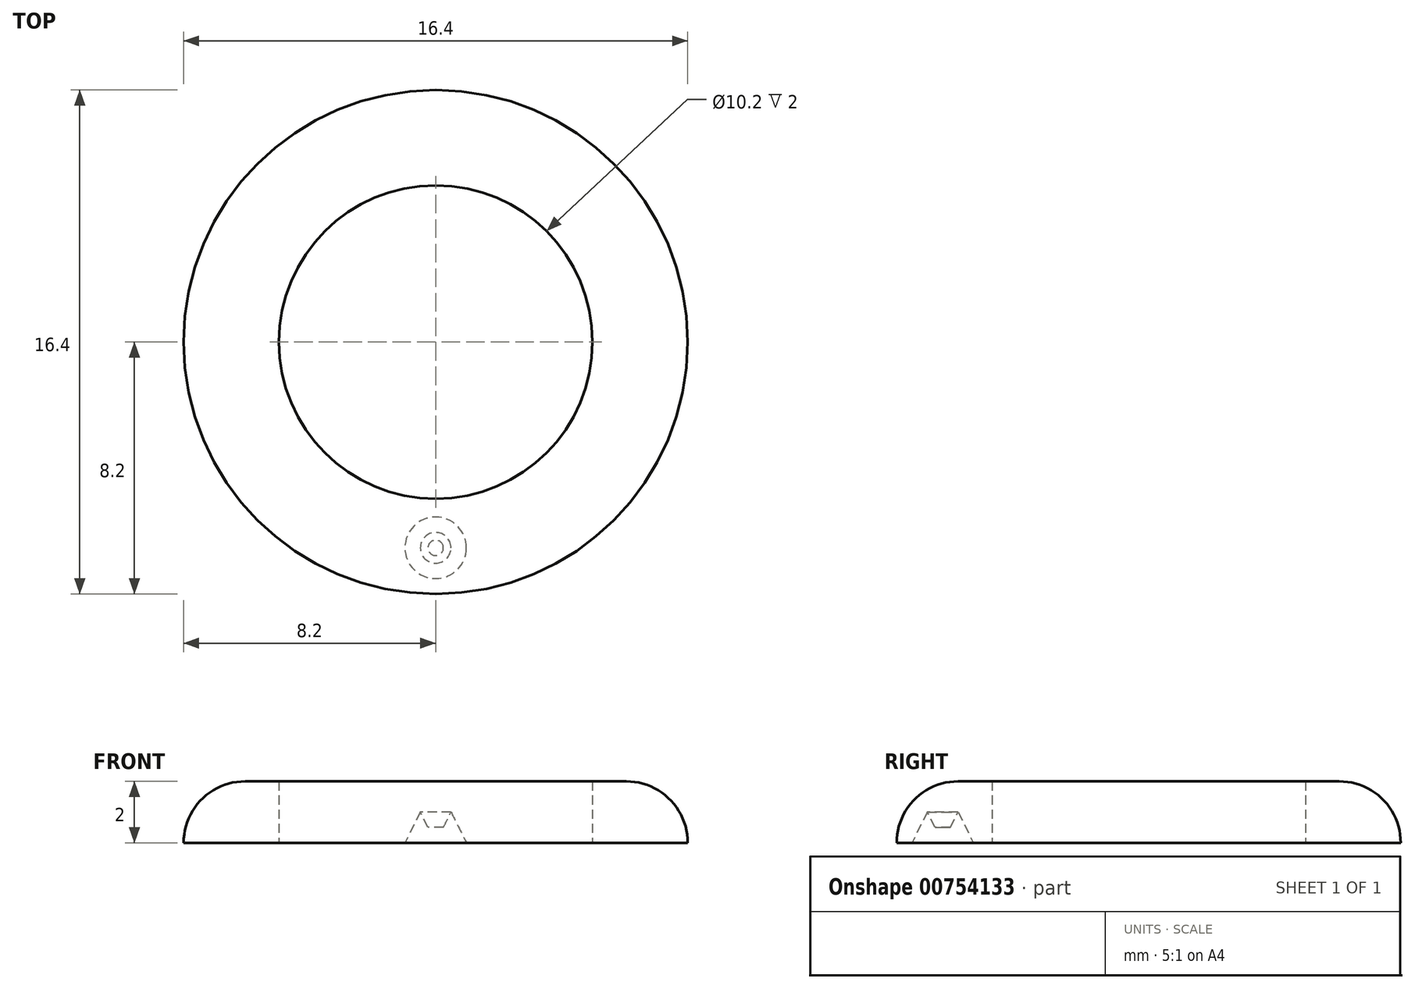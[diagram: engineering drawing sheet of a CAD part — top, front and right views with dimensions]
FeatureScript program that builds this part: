
annotation { "Feature Type Name" : "Feature", "Feature Type Description" : "" }
export const myFeature = defineFeature(function(context is Context, id is Id, definition is map)
    precondition{}
    {
        {
            var Q0;
            Q0=qCreatedBy(makeId("Right.planeOp"),FACE);
            var sketch = newSketch(context, id + "F0", { "sketchPlane" : qUnion([Q0])});
            skLineSegment(sketch, "E0", {"start": v(5.1, 0) * mm, "end": v(8.2, 0) * mm});
            skLineSegment(sketch, "E1", {"start": v(5.1, 0) * mm, "end": v(5.1, 2) * mm});
            skArc(sketch, "E2", {"start": v(8.2, 0) * mm, "mid": v(7.61, 1.41) * mm, "end": v(6.2, 2) * mm});
            skLineSegment(sketch, "E3", {"start": v(5.1, 2) * mm, "end": v(6.2, 2) * mm});
            skLineSegment(sketch, "E4", {"start": v(0, 0) * mm, "end": v(0, 2) * mm, "construction": true});
            skSolve(sketch);
        }
        {
            var Q0;
            Q0=makeQuery(id+"F0.imprint","IMPRINT",FACE,{"disambiguationData":[TD([[makeQuery(id+"F0.imprint","IMPRINT",EDGE,{"derivedFrom":sQuery(id+"F0.wireOp",EDGE,"E0")}),1.0]])]});
            var Q1;
            Q1=sQuery(id+"F0.wireOp",EDGE,"E4");
            var Q2;
            Q2=sQuery(id+"F0.wireOp",EDGE,"E4");
            revolve(context, id + "F1", {"surfaceOperationType" : NewSurfaceOperationType.NEW, "entities" : qUnion([Q0]), "surfaceEntities" : qUnion([Q1]), "axis" : qUnion([Q2]), "revolveType" : RevolveType.FULL});
        }
        {
            var Q0;
            Q0=qCreatedBy(makeId("Right.planeOp"),FACE);
            var sketch = newSketch(context, id + "F2", { "sketchPlane" : qUnion([Q0])});
            skLineSegment(sketch, "E5", {"start": v(-6.7, 0.5) * mm, "end": v(-6.45, 0.5) * mm});
            skLineSegment(sketch, "E6", {"start": v(-6.45, 0.5) * mm, "end": v(-6.2, 1) * mm});
            skLineSegment(sketch, "E7", {"start": v(-6.2, 1) * mm, "end": v(-5.7, 0) * mm});
            skLineSegment(sketch, "E8", {"start": v(-5.7, 0) * mm, "end": v(-6.7, 0) * mm});
            skLineSegment(sketch, "E9", {"start": v(-6.7, 0) * mm, "end": v(-6.7, 0.5) * mm});
            skLineSegment(sketch, "E10", {"start": v(0, 0) * mm, "end": v(0, 2.59) * mm, "construction": true});
            skSolve(sketch);
        }
        {
            var Q0;
            Q0 = qSketchRegion(id + "F2", true);
            var Q1;
            Q1=sQuery(id+"F2.wireOp",EDGE,"E9");
            revolve(context, id + "F3", {"operationType" : NewBodyOperationType.REMOVE, "surfaceOperationType" : NewSurfaceOperationType.NEW, "entities" : qUnion([Q0]), "axis" : qUnion([Q1]), "revolveType" : RevolveType.FULL, "oppositeDirection" : true});
        }
    });
